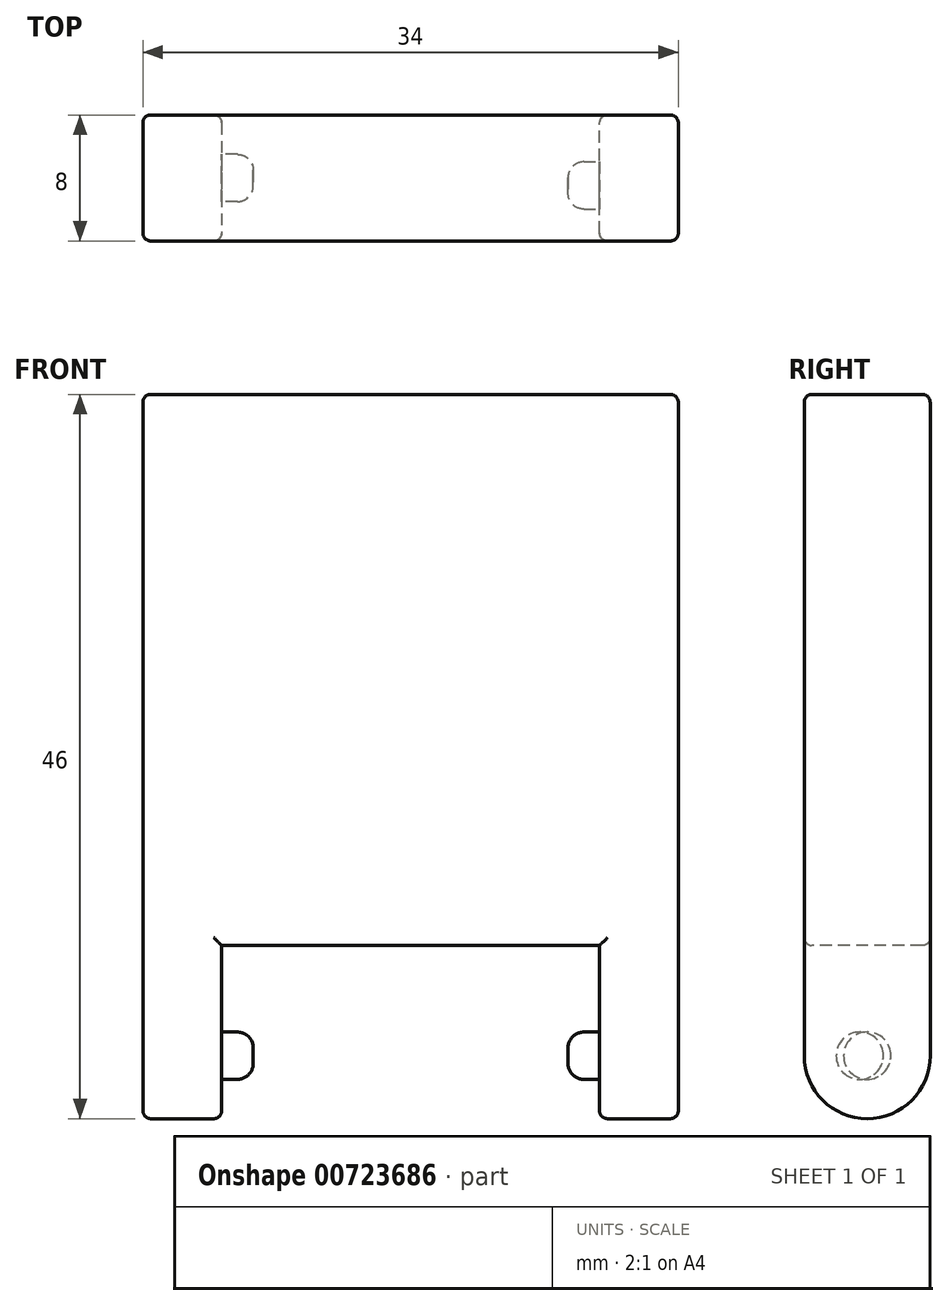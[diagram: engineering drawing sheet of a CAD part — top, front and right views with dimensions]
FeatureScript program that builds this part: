
annotation { "Feature Type Name" : "Feature", "Feature Type Description" : "" }
export const myFeature = defineFeature(function(context is Context, id is Id, definition is map)
    precondition{}
    {
        {
            var Q0;
            Q0=qCreatedBy(makeId("Front.planeOp"),FACE);
            var sketch = newSketch(context, id + "F0", { "sketchPlane" : qUnion([Q0])});
            skLineSegment(sketch, "E0.bottom", {"start": v(0, 0) * mm, "end": v(34, 0) * mm});
            skLineSegment(sketch, "E0.top", {"start": v(0, 35) * mm, "end": v(34, 35) * mm});
            skLineSegment(sketch, "E0.left", {"start": v(0, 0) * mm, "end": v(0, 35) * mm});
            skLineSegment(sketch, "E0.right", {"start": v(34, 0) * mm, "end": v(34, 35) * mm});
            skSolve(sketch);
        }
        {
            var Q0;
            Q0 = qSketchRegion(id + "F0", true);
            extrude(context, id + "F1", {"entities" : qUnion([Q0]), "oppositeDirection" : true, "depth" : 8 * mm, "offsetDistance" : 25 * mm});
        }
        {
            var Q0;
            Q0=makeQuery(id+"F1.opExtrude","SWEPT_FACE",FACE,{"disambiguationData":[OSD([sQuery(id+"F0.wireOp",EDGE,"E0.bottom")])]});
            var sketch = newSketch(context, id + "F2", { "sketchPlane" : qUnion([Q0])});
            skLineSegment(sketch, "E1.bottom", {"start": v(0, -8) * mm, "end": v(5, -8) * mm});
            skLineSegment(sketch, "E1.top", {"start": v(0, 0) * mm, "end": v(5, 0) * mm});
            skLineSegment(sketch, "E1.left", {"start": v(0, -8) * mm, "end": v(0, 0) * mm});
            skLineSegment(sketch, "E1.right", {"start": v(5, -8) * mm, "end": v(5, 0) * mm});
            skLineSegment(sketch, "E2.bottom", {"start": v(34, 0) * mm, "end": v(29, 0) * mm});
            skLineSegment(sketch, "E2.top", {"start": v(34, -8) * mm, "end": v(29, -8) * mm});
            skLineSegment(sketch, "E2.left", {"start": v(34, 0) * mm, "end": v(34, -8) * mm});
            skLineSegment(sketch, "E2.right", {"start": v(29, 0) * mm, "end": v(29, -8) * mm});
            skSolve(sketch);
        }
        {
            var Q0;
            Q0=makeQuery(id+"F2.imprint","IMPRINT",FACE,{"disambiguationData":[TD([[makeQuery(id+"F2.imprint","IMPRINT",EDGE,{"derivedFrom":sQuery(id+"F2.wireOp",EDGE,"E2.bottom")}),-1.0]])]});
            var Q1;
            Q1=makeQuery(id+"F2.imprint","IMPRINT",FACE,{"disambiguationData":[TD([[makeQuery(id+"F2.imprint","IMPRINT",EDGE,{"derivedFrom":sQuery(id+"F2.wireOp",EDGE,"E1.bottom")}),1.0]])]});
            extrude(context, id + "F3", {"entities" : qUnion([Q0, Q1]), "operationType" : NewBodyOperationType.ADD, "depth" : 11 * mm, "offsetDistance" : 25 * mm});
        }
        {
            var Q0;
            Q0=makeQuery(id+"F3.opExtrude","CAP_EDGE",EDGE,{"disambiguationData":[OSD([sQuery(id+"F2.wireOp",EDGE,"E1.top")])],"isStart":false});
            var Q1;
            Q1=makeQuery(id+"F3.opExtrude","CAP_EDGE",EDGE,{"disambiguationData":[OSD([sQuery(id+"F2.wireOp",EDGE,"E1.bottom")])],"isStart":false});
            var Q2;
            Q2=makeQuery(id+"F3.opExtrude","CAP_EDGE",EDGE,{"disambiguationData":[OSD([sQuery(id+"F2.wireOp",EDGE,"E2.top")])],"isStart":false});
            var Q3;
            Q3=makeQuery(id+"F3.opExtrude","CAP_EDGE",EDGE,{"disambiguationData":[OSD([sQuery(id+"F2.wireOp",EDGE,"E2.bottom")])],"isStart":false});
            fillet(context, id + "F4", {"entities" : qUnion([Q0, Q1, Q2, Q3]), "radius" : 4 * mm, "tangentPropagation" : true, "allowEdgeOverflow" : false});
        }
        {
            var Q0;
            Q0=makeQuery(id+"F3.opExtrude","SWEPT_FACE",FACE,{"disambiguationData":[OSD([sQuery(id+"F2.wireOp",EDGE,"E2.right")])]});
            var sketch = newSketch(context, id + "F5", { "sketchPlane" : qUnion([Q0])});
            skCircle(sketch, "E3", {"center": v(-3.53, -7) * mm, "radius": 1.5 * mm});
            skLineSegment(sketch, "E4", {"start": v(-8, -7) * mm, "end": v(0, -7) * mm});
            skSolve(sketch);
        }
        {
            var Q0;
            Q0 = qSketchRegion(id + "F5", true);
            extrude(context, id + "F6", {"entities" : qUnion([Q0]), "operationType" : NewBodyOperationType.ADD, "depth" : 2 * mm, "offsetDistance" : 25 * mm});
        }
        {
            var Q0;
            Q0=makeQuery(id+"F6.opExtrude","CAP_EDGE",EDGE,{"disambiguationData":[OSD([sQuery(id+"F5.wireOp",EDGE,"E3")])],"isStart":false});
            fillet(context, id + "F7", {"entities" : qUnion([Q0]), "radius" : 1 * mm, "tangentPropagation" : true, "allowEdgeOverflow" : false});
        }
        {
            var Q0;
            Q0=makeQuery(id+"F3.opExtrude","SWEPT_FACE",FACE,{"disambiguationData":[OSD([sQuery(id+"F2.wireOp",EDGE,"E1.right")])]});
            var sketch = newSketch(context, id + "F8", { "sketchPlane" : qUnion([Q0])});
            skCircle(sketch, "E5", {"center": v(4, -7) * mm, "radius": 1.5 * mm});
            skLineSegment(sketch, "E6", {"start": v(0, -7) * mm, "end": v(8, -7) * mm});
            skSolve(sketch);
        }
        {
            var Q0;
            Q0 = qSketchRegion(id + "F8", true);
            extrude(context, id + "F9", {"entities" : qUnion([Q0]), "operationType" : NewBodyOperationType.ADD, "depth" : 2 * mm, "offsetDistance" : 25 * mm});
        }
        {
            var Q0;
            Q0=makeQuery(id+"F9.opExtrude","CAP_EDGE",EDGE,{"disambiguationData":[OSD([sQuery(id+"F8.wireOp",EDGE,"E5")])],"isStart":false});
            fillet(context, id + "F10", {"entities" : qUnion([Q0]), "radius" : 1 * mm, "tangentPropagation" : true, "allowEdgeOverflow" : false});
        }
        {
            var Q0;
            Q0=makeQuery(id+"F3.boolean.opBoolean","MERGE",FACE,{"derivedFrom":[makeQuery(id+"F1.opExtrude","CAP_FACE",FACE,{"disambiguationData":[OSD([sQuery(id+"F0.wireOp",EDGE,"E0.bottom"),sQuery(id+"F0.wireOp",EDGE,"E0.top"),sQuery(id+"F0.wireOp",EDGE,"E0.left"),sQuery(id+"F0.wireOp",EDGE,"E0.right")])],"isStart":true}),makeQuery(id+"F3.opExtrude","SWEPT_FACE",FACE,{"disambiguationData":[OSD([sQuery(id+"F2.wireOp",EDGE,"E1.top")])]}),makeQuery(id+"F3.opExtrude","SWEPT_FACE",FACE,{"disambiguationData":[OSD([sQuery(id+"F2.wireOp",EDGE,"E2.bottom")])]})]});
            var Q1;
            Q1=makeQuery(id+"F3.boolean.opBoolean","MERGE",FACE,{"derivedFrom":[makeQuery(id+"F1.opExtrude","CAP_FACE",FACE,{"disambiguationData":[OSD([sQuery(id+"F0.wireOp",EDGE,"E0.bottom"),sQuery(id+"F0.wireOp",EDGE,"E0.top"),sQuery(id+"F0.wireOp",EDGE,"E0.left"),sQuery(id+"F0.wireOp",EDGE,"E0.right")])],"isStart":false}),makeQuery(id+"F3.opExtrude","SWEPT_FACE",FACE,{"disambiguationData":[OSD([sQuery(id+"F2.wireOp",EDGE,"E1.bottom")])]}),makeQuery(id+"F3.opExtrude","SWEPT_FACE",FACE,{"disambiguationData":[OSD([sQuery(id+"F2.wireOp",EDGE,"E2.top")])]})]});
            var Q2;
            Q2=makeQuery(id+"F1.opExtrude","SWEPT_FACE",FACE,{"disambiguationData":[OSD([sQuery(id+"F0.wireOp",EDGE,"E0.top")])]});
            fillet(context, id + "F11", {"entities" : qUnion([Q0, Q1, Q2]), "radius" : 0.5 * mm, "tangentPropagation" : true, "allowEdgeOverflow" : false});
        }
    });
